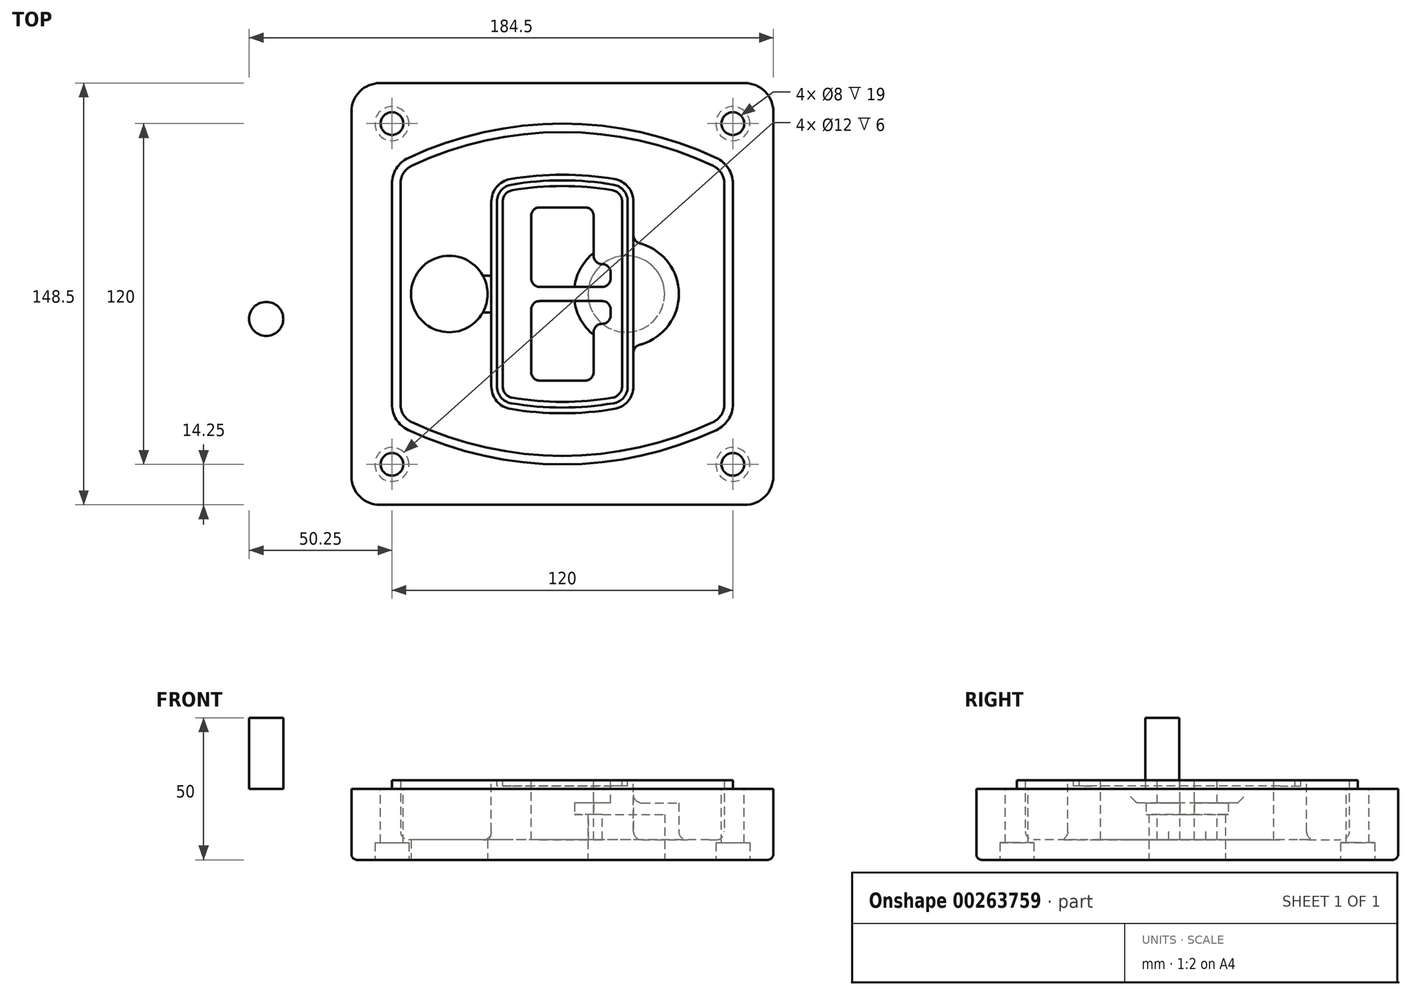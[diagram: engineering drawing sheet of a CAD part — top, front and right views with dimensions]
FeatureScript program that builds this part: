
annotation { "Feature Type Name" : "Feature", "Feature Type Description" : "" }
export const myFeature = defineFeature(function(context is Context, id is Id, definition is map)
    precondition{}
    {
        {
            var Q0;
            Q0=qCreatedBy(makeId("Top.planeOp"),FACE);
            var sketch = newSketch(context, id + "F0", { "sketchPlane" : qUnion([Q0])});
            skPoint(sketch, "E0.rect.middle", {"position": v(0, 0) * mm});
            skLineSegment(sketch, "E1.bottom", {"start": v(-64.25, -74.25) * mm, "end": v(64.25, -74.25) * mm});
            skLineSegment(sketch, "E1.top", {"start": v(-64.25, 74.25) * mm, "end": v(64.25, 74.25) * mm});
            skLineSegment(sketch, "E1.left", {"start": v(-74.25, -64.25) * mm, "end": v(-74.25, 64.25) * mm});
            skLineSegment(sketch, "E1.right", {"start": v(74.25, -64.25) * mm, "end": v(74.25, 64.25) * mm});
            skLineSegment(sketch, "E2", {"start": v(-74.25, 74.25) * mm, "end": v(74.25, -74.25) * mm, "construction": true});
            skLineSegment(sketch, "E3", {"start": v(74.25, 74.25) * mm, "end": v(-74.25, -74.25) * mm, "construction": true});
            skCircle(sketch, "E4", {"center": v(-60, 60) * mm, "radius": 4 * mm});
            skCircle(sketch, "E5", {"center": v(60, 60) * mm, "radius": 4 * mm});
            skCircle(sketch, "E6", {"center": v(60, -60) * mm, "radius": 4 * mm});
            skCircle(sketch, "E7", {"center": v(-60, -60) * mm, "radius": 4 * mm});
            skLineSegment(sketch, "E8", {"start": v(-60, 60) * mm, "end": v(60, 60) * mm, "construction": true});
            skLineSegment(sketch, "E9", {"start": v(60, 60) * mm, "end": v(60, -60) * mm, "construction": true});
            skLineSegment(sketch, "E10", {"start": v(60, -60) * mm, "end": v(-60, -60) * mm, "construction": true});
            skLineSegment(sketch, "E11", {"start": v(-60, -60) * mm, "end": v(-60, 60) * mm, "construction": true});
            skLineSegment(sketch, "E12", {"start": v(-60, 38.83) * mm, "end": v(-60, -38.83) * mm});
            skLineSegment(sketch, "E13", {"start": v(60, 38.83) * mm, "end": v(60, -38.83) * mm});
            skArc(sketch, "E14", {"start": v(54.26, 47.88) * mm, "mid": v(0, 60) * mm, "end": v(-54.26, 47.88) * mm});
            skArc(sketch, "E15", {"start": v(-54.26, -47.88) * mm, "mid": v(0, -60) * mm, "end": v(54.26, -47.88) * mm});
            skLineSegment(sketch, "E16", {"start": v(-60, 0) * mm, "end": v(60, 0) * mm, "construction": true});
            skPoint(sketch, "E17.visualSharp", {"position": v(-60, -45) * mm});
            skArc(sketch, "E17.filletArc", {"start": v(-60, -38.83) * mm, "mid": v(-58.44, -44.2) * mm, "end": v(-54.26, -47.88) * mm});
            skPoint(sketch, "E18.visualSharp", {"position": v(-60, 45) * mm});
            skArc(sketch, "E18.filletArc", {"start": v(-54.26, 47.88) * mm, "mid": v(-58.44, 44.2) * mm, "end": v(-60, 38.83) * mm});
            skPoint(sketch, "E19.visualSharp", {"position": v(60, 45) * mm});
            skArc(sketch, "E19.filletArc", {"start": v(60, 38.83) * mm, "mid": v(58.44, 44.2) * mm, "end": v(54.26, 47.88) * mm});
            skPoint(sketch, "E20.visualSharp", {"position": v(60, -45) * mm});
            skArc(sketch, "E20.filletArc", {"start": v(54.26, -47.88) * mm, "mid": v(58.44, -44.2) * mm, "end": v(60, -38.83) * mm});
            skPoint(sketch, "E21.visualSharp", {"position": v(-74.25, 74.25) * mm});
            skArc(sketch, "E21.filletArc", {"start": v(-64.25, 74.25) * mm, "mid": v(-71.32, 71.32) * mm, "end": v(-74.25, 64.25) * mm});
            skPoint(sketch, "E22.visualSharp", {"position": v(74.25, 74.25) * mm});
            skArc(sketch, "E22.filletArc", {"start": v(74.25, 64.25) * mm, "mid": v(71.32, 71.32) * mm, "end": v(64.25, 74.25) * mm});
            skPoint(sketch, "E23.visualSharp", {"position": v(74.25, -74.25) * mm});
            skArc(sketch, "E23.filletArc", {"start": v(64.25, -74.25) * mm, "mid": v(71.32, -71.32) * mm, "end": v(74.25, -64.25) * mm});
            skPoint(sketch, "E24.visualSharp", {"position": v(-74.25, -74.25) * mm});
            skArc(sketch, "E24.filletArc", {"start": v(-74.25, -64.25) * mm, "mid": v(-71.32, -71.32) * mm, "end": v(-64.25, -74.25) * mm});
            skArc(sketch, "E25.0", {"start": v(57, 38.83) * mm, "mid": v(55.9, 42.58) * mm, "end": v(52.98, 45.17) * mm});
            skLineSegment(sketch, "E25.1", {"start": v(57, 38.83) * mm, "end": v(57, -38.83) * mm});
            skArc(sketch, "E25.2", {"start": v(52.98, -45.17) * mm, "mid": v(55.9, -42.58) * mm, "end": v(57, -38.83) * mm});
            skArc(sketch, "E25.3", {"start": v(-52.98, -45.17) * mm, "mid": v(0, -57) * mm, "end": v(52.98, -45.17) * mm});
            skArc(sketch, "E25.4", {"start": v(-57, -38.83) * mm, "mid": v(-55.9, -42.58) * mm, "end": v(-52.98, -45.17) * mm});
            skArc(sketch, "E25.5", {"start": v(52.98, 45.17) * mm, "mid": v(0, 57) * mm, "end": v(-52.98, 45.17) * mm});
            skLineSegment(sketch, "E25.6", {"start": v(-57, 38.83) * mm, "end": v(-57, -38.83) * mm});
            skArc(sketch, "E25.7", {"start": v(-52.98, 45.17) * mm, "mid": v(-55.9, 42.58) * mm, "end": v(-57, 38.83) * mm});
            skArc(sketch, "E26.0", {"start": v(-55.96, 51.5) * mm, "mid": v(-61.82, 46.33) * mm, "end": v(-64, 38.83) * mm});
            skArc(sketch, "E26.1", {"start": v(55.96, 51.5) * mm, "mid": v(0, 64) * mm, "end": v(-55.96, 51.5) * mm});
            skArc(sketch, "E26.2", {"start": v(64, 38.83) * mm, "mid": v(61.82, 46.33) * mm, "end": v(55.96, 51.5) * mm});
            skLineSegment(sketch, "E26.3", {"start": v(64, 38.83) * mm, "end": v(64, -38.83) * mm});
            skArc(sketch, "E26.4", {"start": v(55.96, -51.5) * mm, "mid": v(61.82, -46.33) * mm, "end": v(64, -38.83) * mm});
            skLineSegment(sketch, "E26.5", {"start": v(-64, 38.83) * mm, "end": v(-64, -38.83) * mm});
            skArc(sketch, "E26.6", {"start": v(-55.96, -51.5) * mm, "mid": v(0, -64) * mm, "end": v(55.96, -51.5) * mm});
            skArc(sketch, "E26.7", {"start": v(-64, -38.83) * mm, "mid": v(-61.82, -46.33) * mm, "end": v(-55.96, -51.5) * mm});
            skSolve(sketch);
        }
        {
            var Q0;
            Q0=makeQuery(id+"F0.imprint","IMPRINT",FACE,{"disambiguationData":[TD([[makeQuery(id+"F0.imprint","IMPRINT",EDGE,{"derivedFrom":sQuery(id+"F0.wireOp",EDGE,"E1.bottom")}),1.0]])]});
            var Q1;
            Q1=makeQuery(id+"F0.imprint","IMPRINT",FACE,{"disambiguationData":[TD([[makeQuery(id+"F0.imprint","IMPRINT",EDGE,{"derivedFrom":sQuery(id+"F0.wireOp",EDGE,"E12")}),1.0]])]});
            var Q2;
            Q2=makeQuery(id+"F0.imprint","IMPRINT",FACE,{"disambiguationData":[TD([[makeQuery(id+"F0.imprint","IMPRINT",EDGE,{"derivedFrom":sQuery(id+"F0.wireOp",EDGE,"E25.0")}),1.0]])]});
            var Q3;
            Q3=makeQuery(id+"F0.imprint","IMPRINT",FACE,{"disambiguationData":[TD([[makeQuery(id+"F0.imprint","IMPRINT",EDGE,{"derivedFrom":sQuery(id+"F0.wireOp",EDGE,"E12")}),-1.0]])]});
            extrude(context, id + "F1", {"entities" : qUnion([Q0, Q1, Q2, Q3]), "oppositeDirection" : true, "depth" : 25 * mm});
        }
        {
            var Q0;
            Q0=makeQuery(id+"F0.imprint","IMPRINT",FACE,{"disambiguationData":[TD([[makeQuery(id+"F0.imprint","IMPRINT",EDGE,{"derivedFrom":sQuery(id+"F0.wireOp",EDGE,"E12")}),1.0]])]});
            extrude(context, id + "F2", {"entities" : qUnion([Q0]), "operationType" : NewBodyOperationType.ADD, "depth" : 3 * mm});
        }
        {
            var Q0;
            Q0=makeQuery(id+"F0.imprint","IMPRINT",FACE,{"disambiguationData":[TD([[makeQuery(id+"F0.imprint","IMPRINT",EDGE,{"derivedFrom":sQuery(id+"F0.wireOp",EDGE,"E25.0")}),1.0]])]});
            extrude(context, id + "F3", {"entities" : qUnion([Q0]), "operationType" : NewBodyOperationType.REMOVE, "oppositeDirection" : true, "depth" : 18 * mm});
        }
        {
            var Q0;
            Q0=makeQuery(id+"F2.opExtrude","CAP_FACE",FACE,{"disambiguationData":[OSD([sQuery(id+"F0.wireOp",EDGE,"E12"),sQuery(id+"F0.wireOp",EDGE,"E13"),sQuery(id+"F0.wireOp",EDGE,"E14"),sQuery(id+"F0.wireOp",EDGE,"E15"),sQuery(id+"F0.wireOp",EDGE,"E17.filletArc"),sQuery(id+"F0.wireOp",EDGE,"E18.filletArc"),sQuery(id+"F0.wireOp",EDGE,"E19.filletArc"),sQuery(id+"F0.wireOp",EDGE,"E20.filletArc"),sQuery(id+"F0.wireOp",EDGE,"E25.0"),sQuery(id+"F0.wireOp",EDGE,"E25.1"),sQuery(id+"F0.wireOp",EDGE,"E25.2"),sQuery(id+"F0.wireOp",EDGE,"E25.3"),sQuery(id+"F0.wireOp",EDGE,"E25.4"),sQuery(id+"F0.wireOp",EDGE,"E25.5"),sQuery(id+"F0.wireOp",EDGE,"E25.6"),sQuery(id+"F0.wireOp",EDGE,"E25.7")])],"isStart":false});
            var sketch = newSketch(context, id + "F4", { "sketchPlane" : qUnion([Q0])});
            skArc(sketch, "E27.0", {"start": v(-18.34, -40.45) * mm, "mid": v(0, -42) * mm, "end": v(18.34, -40.45) * mm});
            skArc(sketch, "E28.0", {"start": v(18.34, 40.45) * mm, "mid": v(0, 42) * mm, "end": v(-18.34, 40.45) * mm});
            skLineSegment(sketch, "E29", {"start": v(-25, 32.57) * mm, "end": v(-25, -32.57) * mm});
            skLineSegment(sketch, "E30", {"start": v(25, 32.57) * mm, "end": v(25, -32.57) * mm});
            skLineSegment(sketch, "E31", {"start": v(-25, 39.1) * mm, "end": v(25, 39.1) * mm, "construction": true});
            skLineSegment(sketch, "E32", {"start": v(-25, -39.1) * mm, "end": v(25, -39.1) * mm, "construction": true});
            skPoint(sketch, "E33.visualSharp", {"position": v(-25, 39.1) * mm});
            skArc(sketch, "E33.filletArc", {"start": v(-18.34, 40.45) * mm, "mid": v(-23.11, 37.73) * mm, "end": v(-25, 32.57) * mm});
            skPoint(sketch, "E34.visualSharp", {"position": v(25, 39.1) * mm});
            skArc(sketch, "E34.filletArc", {"start": v(25, 32.57) * mm, "mid": v(23.11, 37.73) * mm, "end": v(18.34, 40.45) * mm});
            skPoint(sketch, "E35.visualSharp", {"position": v(25, -39.1) * mm});
            skArc(sketch, "E35.filletArc", {"start": v(18.34, -40.45) * mm, "mid": v(23.11, -37.73) * mm, "end": v(25, -32.57) * mm});
            skPoint(sketch, "E36.visualSharp", {"position": v(-25, -39.1) * mm});
            skArc(sketch, "E36.filletArc", {"start": v(-25, -32.57) * mm, "mid": v(-23.11, -37.73) * mm, "end": v(-18.34, -40.45) * mm});
            skArc(sketch, "E37.0", {"start": v(52.98, 45.17) * mm, "mid": v(0, 57) * mm, "end": v(-52.98, 45.17) * mm});
            skArc(sketch, "E37.1", {"start": v(-52.98, 45.17) * mm, "mid": v(-55.9, 42.58) * mm, "end": v(-57, 38.83) * mm});
            skLineSegment(sketch, "E37.2", {"start": v(-57, 38.83) * mm, "end": v(-57, -38.83) * mm});
            skArc(sketch, "E37.3", {"start": v(-57, -38.83) * mm, "mid": v(-55.9, -42.58) * mm, "end": v(-52.98, -45.17) * mm});
            skArc(sketch, "E37.4", {"start": v(-52.98, -45.17) * mm, "mid": v(0, -57) * mm, "end": v(52.98, -45.17) * mm});
            skArc(sketch, "E37.5", {"start": v(52.98, -45.17) * mm, "mid": v(55.9, -42.58) * mm, "end": v(57, -38.83) * mm});
            skLineSegment(sketch, "E37.6", {"start": v(57, 38.83) * mm, "end": v(57, -38.83) * mm});
            skArc(sketch, "E37.7", {"start": v(57, 38.83) * mm, "mid": v(55.9, 42.58) * mm, "end": v(52.98, 45.17) * mm});
            skLineSegment(sketch, "E38.0", {"start": v(23, 32.57) * mm, "end": v(23, -32.57) * mm});
            skArc(sketch, "E38.1", {"start": v(18, -38.48) * mm, "mid": v(21.58, -36.44) * mm, "end": v(23, -32.57) * mm});
            skArc(sketch, "E38.2", {"start": v(-18, -38.48) * mm, "mid": v(0, -40) * mm, "end": v(18, -38.48) * mm});
            skArc(sketch, "E38.3", {"start": v(-23, -32.57) * mm, "mid": v(-21.58, -36.44) * mm, "end": v(-18, -38.48) * mm});
            skLineSegment(sketch, "E38.4", {"start": v(-23, 32.57) * mm, "end": v(-23, -32.57) * mm});
            skArc(sketch, "E38.5", {"start": v(23, 32.57) * mm, "mid": v(21.58, 36.44) * mm, "end": v(18, 38.48) * mm});
            skArc(sketch, "E38.6", {"start": v(-18, 38.48) * mm, "mid": v(-21.58, 36.44) * mm, "end": v(-23, 32.57) * mm});
            skArc(sketch, "E38.7", {"start": v(18, 38.48) * mm, "mid": v(0, 40) * mm, "end": v(-18, 38.48) * mm});
            skArc(sketch, "E39.0", {"start": v(21, 32.57) * mm, "mid": v(20.06, 35.15) * mm, "end": v(17.67, 36.5) * mm});
            skLineSegment(sketch, "E39.1", {"start": v(21, 32.57) * mm, "end": v(21, -32.57) * mm});
            skArc(sketch, "E39.2", {"start": v(17.67, -36.5) * mm, "mid": v(20.06, -35.15) * mm, "end": v(21, -32.57) * mm});
            skArc(sketch, "E39.3", {"start": v(-17.67, -36.5) * mm, "mid": v(0, -38) * mm, "end": v(17.67, -36.5) * mm});
            skArc(sketch, "E39.4", {"start": v(-21, -32.57) * mm, "mid": v(-20.06, -35.15) * mm, "end": v(-17.67, -36.5) * mm});
            skArc(sketch, "E39.5", {"start": v(17.67, 36.5) * mm, "mid": v(0, 38) * mm, "end": v(-17.67, 36.5) * mm});
            skLineSegment(sketch, "E39.6", {"start": v(-21, 32.57) * mm, "end": v(-21, -32.57) * mm});
            skArc(sketch, "E39.7", {"start": v(-17.67, 36.5) * mm, "mid": v(-20.06, 35.15) * mm, "end": v(-21, 32.57) * mm});
            skLineSegment(sketch, "E40", {"start": v(-25, 0) * mm, "end": v(25, 0) * mm, "construction": true});
            skLineSegment(sketch, "E41", {"start": v(-11, 5.5) * mm, "end": v(-11, 27.5) * mm});
            skLineSegment(sketch, "E42", {"start": v(-8, 30.5) * mm, "end": v(8, 30.5) * mm});
            skLineSegment(sketch, "E43", {"start": v(11, 27.5) * mm, "end": v(11, 13.5) * mm});
            skLineSegment(sketch, "E44", {"start": v(14, 10.5) * mm, "end": v(14, 10.5) * mm});
            skLineSegment(sketch, "E45", {"start": v(17, 7.5) * mm, "end": v(17, 5.5) * mm});
            skLineSegment(sketch, "E46", {"start": v(14, 2.5) * mm, "end": v(-8, 2.5) * mm});
            skPoint(sketch, "E47.visualSharp", {"position": v(-11, 30.5) * mm});
            skArc(sketch, "E47.filletArc", {"start": v(-8, 30.5) * mm, "mid": v(-10.12, 29.62) * mm, "end": v(-11, 27.5) * mm});
            skPoint(sketch, "E48.visualSharp", {"position": v(11, 30.5) * mm});
            skArc(sketch, "E48.filletArc", {"start": v(11, 27.5) * mm, "mid": v(10.12, 29.62) * mm, "end": v(8, 30.5) * mm});
            skPoint(sketch, "E49.visualSharp", {"position": v(11, 10.5) * mm});
            skArc(sketch, "E49.filletArc", {"start": v(11, 13.5) * mm, "mid": v(11.88, 11.38) * mm, "end": v(14, 10.5) * mm});
            skPoint(sketch, "E50.visualSharp", {"position": v(17, 10.5) * mm});
            skArc(sketch, "E50.filletArc", {"start": v(17, 7.5) * mm, "mid": v(16.12, 9.62) * mm, "end": v(14, 10.5) * mm});
            skPoint(sketch, "E51.visualSharp", {"position": v(17, 2.5) * mm});
            skArc(sketch, "E51.filletArc", {"start": v(14, 2.5) * mm, "mid": v(16.12, 3.38) * mm, "end": v(17, 5.5) * mm});
            skPoint(sketch, "E52.visualSharp", {"position": v(-11, 2.5) * mm});
            skArc(sketch, "E52.filletArc", {"start": v(-11, 5.5) * mm, "mid": v(-10.12, 3.38) * mm, "end": v(-8, 2.5) * mm});
            skLineSegment(sketch, "E53.0.MirrorCS", {"start": v(14, -2.5) * mm, "end": v(-8, -2.5) * mm});
            skArc(sketch, "E54.0.MirrorCS", {"start": v(-11, -5.5) * mm, "mid": v(-10.12, -3.38) * mm, "end": v(-8, -2.5) * mm});
            skLineSegment(sketch, "E55.0.MirrorCS", {"start": v(-11, -5.5) * mm, "end": v(-11, -27.5) * mm});
            skArc(sketch, "E56.0.MirrorCS", {"start": v(-8, -30.5) * mm, "mid": v(-10.12, -29.62) * mm, "end": v(-11, -27.5) * mm});
            skLineSegment(sketch, "E57.0.MirrorCS", {"start": v(-8, -30.5) * mm, "end": v(8, -30.5) * mm});
            skArc(sketch, "E58.0.MirrorCS", {"start": v(11, -27.5) * mm, "mid": v(10.12, -29.62) * mm, "end": v(8, -30.5) * mm});
            skLineSegment(sketch, "E59.0.MirrorCS", {"start": v(11, -27.5) * mm, "end": v(11, -13.5) * mm});
            skArc(sketch, "E60.0.MirrorCS", {"start": v(11, -13.5) * mm, "mid": v(11.88, -11.38) * mm, "end": v(14, -10.5) * mm});
            skArc(sketch, "E61.0.MirrorCS", {"start": v(17, -7.5) * mm, "mid": v(16.12, -9.62) * mm, "end": v(14, -10.5) * mm});
            skLineSegment(sketch, "E62.0.MirrorCS", {"start": v(17, -7.5) * mm, "end": v(17, -5.5) * mm});
            skArc(sketch, "E63.0.MirrorCS", {"start": v(14, -2.5) * mm, "mid": v(16.12, -3.38) * mm, "end": v(17, -5.5) * mm});
            skSolve(sketch);
        }
        {
            var Q0;
            Q0=makeQuery(id+"F4.imprint","IMPRINT",FACE,{"disambiguationData":[TD([[makeQuery(id+"F4.imprint","IMPRINT",EDGE,{"derivedFrom":sQuery(id+"F4.wireOp",EDGE,"E27.0")}),1.0]])]});
            var Q1;
            Q1=makeQuery(id+"F4.imprint","IMPRINT",FACE,{"disambiguationData":[TD([[makeQuery(id+"F4.imprint","IMPRINT",EDGE,{"derivedFrom":sQuery(id+"F4.wireOp",EDGE,"E38.0")}),-1.0]])]});
            var Q2;
            Q2=makeQuery(id+"F4.imprint","IMPRINT",FACE,{"disambiguationData":[TD([[makeQuery(id+"F4.imprint","IMPRINT",EDGE,{"derivedFrom":sQuery(id+"F4.wireOp",EDGE,"E39.0")}),1.0]])]});
            extrude(context, id + "F5", {"entities" : qUnion([Q0, Q1, Q2]), "operationType" : NewBodyOperationType.ADD, "endBound" : BoundingType.UP_TO_NEXT, "oppositeDirection" : true, "depth" : 25 * mm});
        }
        {
            var Q0;
            Q0=makeQuery(id+"F4.imprint","IMPRINT",FACE,{"disambiguationData":[TD([[makeQuery(id+"F4.imprint","IMPRINT",EDGE,{"derivedFrom":sQuery(id+"F4.wireOp",EDGE,"E38.0")}),-1.0]])]});
            extrude(context, id + "F6", {"entities" : qUnion([Q0]), "operationType" : NewBodyOperationType.REMOVE, "oppositeDirection" : true, "depth" : 2 * mm});
        }
        {
            var Q0;
            Q0=makeQuery(id+"F1.opExtrude","CAP_FACE",FACE,{"disambiguationData":[OSD([sQuery(id+"F0.wireOp",EDGE,"E1.bottom"),sQuery(id+"F0.wireOp",EDGE,"E1.top"),sQuery(id+"F0.wireOp",EDGE,"E1.left"),sQuery(id+"F0.wireOp",EDGE,"E1.right"),sQuery(id+"F0.wireOp",EDGE,"E4"),sQuery(id+"F0.wireOp",EDGE,"E5"),sQuery(id+"F0.wireOp",EDGE,"E6"),sQuery(id+"F0.wireOp",EDGE,"E7"),sQuery(id+"F0.wireOp",EDGE,"E21.filletArc"),sQuery(id+"F0.wireOp",EDGE,"E22.filletArc"),sQuery(id+"F0.wireOp",EDGE,"E23.filletArc"),sQuery(id+"F0.wireOp",EDGE,"E24.filletArc")])],"isStart":false});
            var sketch = newSketch(context, id + "F7", { "sketchPlane" : qUnion([Q0])});
            skCircle(sketch, "E64", {"center": v(22.5, 0) * mm, "radius": 13.47 * mm});
            skCircle(sketch, "E65", {"center": v(-39.81, 0) * mm, "radius": 13.47 * mm});
            skLineSegment(sketch, "E66", {"start": v(74.25, 0) * mm, "end": v(-74.25, 0) * mm});
            skCircle(sketch, "E67", {"center": v(22.5, 0) * mm, "radius": 18.47 * mm});
            skCircle(sketch, "E68", {"center": v(60, -60) * mm, "radius": 6 * mm});
            skCircle(sketch, "E69", {"center": v(-60, -60) * mm, "radius": 6 * mm});
            skCircle(sketch, "E70", {"center": v(-60, 60) * mm, "radius": 6 * mm});
            skCircle(sketch, "E71", {"center": v(60, 60) * mm, "radius": 6 * mm});
            skSolve(sketch);
        }
        {
            var Q0;
            {var subQ1=sQuery(id+"F7.wireOp",EDGE,"E66");var subQ4=sQuery(id+"F7.wireOp",EDGE,"E64");var subQ6=makeQuery(id+"F7.imprint","INTERSECT",VERTEX,{"disambiguationData":[OD(0.0)],"derivedFrom":[subQ4,subQ1]});Q0=makeQuery(id+"F7.imprint","IMPRINT",FACE,{"disambiguationData":[TD([[makeQuery(id+"F7.imprint","IMPRINT",EDGE,{"disambiguationData":[TD([[subQ6,-1.0]])],"derivedFrom":subQ4}),-1.0]])]});}
            var Q1;
            {var subQ0=sQuery(id+"F7.wireOp",EDGE,"E66");var subQ1=sQuery(id+"F7.wireOp",EDGE,"E64");var subQ3=makeQuery(id+"F7.imprint","INTERSECT",VERTEX,{"disambiguationData":[OD(0.0)],"derivedFrom":[subQ1,subQ0]});Q1=makeQuery(id+"F7.imprint","IMPRINT",FACE,{"disambiguationData":[TD([[makeQuery(id+"F7.imprint","IMPRINT",EDGE,{"disambiguationData":[TD([[subQ3,-1.0]])],"derivedFrom":subQ1}),1.0]])]});}
            var Q2;
            {var subQ0=sQuery(id+"F7.wireOp",EDGE,"E66");var subQ1=sQuery(id+"F7.wireOp",EDGE,"E64");var subQ3=makeQuery(id+"F7.imprint","INTERSECT",VERTEX,{"disambiguationData":[OD(0.0)],"derivedFrom":[subQ1,subQ0]});Q2=makeQuery(id+"F7.imprint","IMPRINT",FACE,{"disambiguationData":[TD([[makeQuery(id+"F7.imprint","IMPRINT",EDGE,{"disambiguationData":[TD([[subQ3,1.0]])],"derivedFrom":subQ1}),1.0]])]});}
            var Q3;
            {var subQ1=sQuery(id+"F7.wireOp",EDGE,"E66");var subQ4=sQuery(id+"F7.wireOp",EDGE,"E64");var subQ6=makeQuery(id+"F7.imprint","INTERSECT",VERTEX,{"disambiguationData":[OD(0.0)],"derivedFrom":[subQ4,subQ1]});Q3=makeQuery(id+"F7.imprint","IMPRINT",FACE,{"disambiguationData":[TD([[makeQuery(id+"F7.imprint","IMPRINT",EDGE,{"disambiguationData":[TD([[subQ6,1.0]])],"derivedFrom":subQ4}),-1.0]])]});}
            extrude(context, id + "F8", {"entities" : qUnion([Q0, Q1, Q2, Q3]), "operationType" : NewBodyOperationType.ADD, "oppositeDirection" : true, "depth" : 20 * mm});
        }
        {
            var Q0;
            {var subQ0=sQuery(id+"F7.wireOp",EDGE,"E66");var subQ1=sQuery(id+"F7.wireOp",EDGE,"E64");var subQ3=makeQuery(id+"F7.imprint","INTERSECT",VERTEX,{"disambiguationData":[OD(0.0)],"derivedFrom":[subQ1,subQ0]});Q0=makeQuery(id+"F7.imprint","IMPRINT",FACE,{"disambiguationData":[TD([[makeQuery(id+"F7.imprint","IMPRINT",EDGE,{"disambiguationData":[TD([[subQ3,-1.0]])],"derivedFrom":subQ1}),1.0]])]});}
            var Q1;
            {var subQ0=sQuery(id+"F7.wireOp",EDGE,"E66");var subQ1=sQuery(id+"F7.wireOp",EDGE,"E64");var subQ3=makeQuery(id+"F7.imprint","INTERSECT",VERTEX,{"disambiguationData":[OD(0.0)],"derivedFrom":[subQ1,subQ0]});Q1=makeQuery(id+"F7.imprint","IMPRINT",FACE,{"disambiguationData":[TD([[makeQuery(id+"F7.imprint","IMPRINT",EDGE,{"disambiguationData":[TD([[subQ3,1.0]])],"derivedFrom":subQ1}),1.0]])]});}
            extrude(context, id + "F9", {"entities" : qUnion([Q0, Q1]), "operationType" : NewBodyOperationType.REMOVE, "oppositeDirection" : true, "depth" : 16 * mm});
        }
        {
            var Q0;
            {var subQ0=sQuery(id+"F7.wireOp",EDGE,"E66");var subQ1=sQuery(id+"F7.wireOp",EDGE,"E65");var subQ3=makeQuery(id+"F7.imprint","INTERSECT",VERTEX,{"disambiguationData":[OD(0.0)],"derivedFrom":[subQ1,subQ0]});Q0=makeQuery(id+"F7.imprint","IMPRINT",FACE,{"disambiguationData":[TD([[makeQuery(id+"F7.imprint","IMPRINT",EDGE,{"disambiguationData":[TD([[subQ3,-1.0]])],"derivedFrom":subQ1}),1.0]])]});}
            var Q1;
            {var subQ0=sQuery(id+"F7.wireOp",EDGE,"E66");var subQ1=sQuery(id+"F7.wireOp",EDGE,"E65");var subQ3=makeQuery(id+"F7.imprint","INTERSECT",VERTEX,{"disambiguationData":[OD(0.0)],"derivedFrom":[subQ1,subQ0]});Q1=makeQuery(id+"F7.imprint","IMPRINT",FACE,{"disambiguationData":[TD([[makeQuery(id+"F7.imprint","IMPRINT",EDGE,{"disambiguationData":[TD([[subQ3,1.0]])],"derivedFrom":subQ1}),1.0]])]});}
            extrude(context, id + "F10", {"entities" : qUnion([Q0, Q1]), "operationType" : NewBodyOperationType.REMOVE, "oppositeDirection" : true, "depth" : 25 * mm});
        }
        {
            var Q0;
            Q0=makeQuery(id+"F7.imprint","IMPRINT",FACE,{"disambiguationData":[TD([[makeQuery(id+"F7.imprint","IMPRINT",EDGE,{"derivedFrom":sQuery(id+"F7.wireOp",EDGE,"E68")}),1.0]])]});
            var Q1;
            Q1=makeQuery(id+"F7.imprint","IMPRINT",FACE,{"disambiguationData":[TD([[makeQuery(id+"F7.imprint","IMPRINT",EDGE,{"derivedFrom":makeQuery(id+"F1.opExtrude","CAP_EDGE",EDGE,{"disambiguationData":[OSD([sQuery(id+"F0.wireOp",EDGE,"E5")])],"isStart":false})}),-1.0]])]});
            var Q2;
            Q2=makeQuery(id+"F7.imprint","IMPRINT",FACE,{"disambiguationData":[TD([[makeQuery(id+"F7.imprint","IMPRINT",EDGE,{"derivedFrom":sQuery(id+"F7.wireOp",EDGE,"E69")}),1.0]])]});
            var Q3;
            Q3=makeQuery(id+"F7.imprint","IMPRINT",FACE,{"disambiguationData":[TD([[makeQuery(id+"F7.imprint","IMPRINT",EDGE,{"derivedFrom":makeQuery(id+"F1.opExtrude","CAP_EDGE",EDGE,{"disambiguationData":[OSD([sQuery(id+"F0.wireOp",EDGE,"E4")])],"isStart":false})}),-1.0]])]});
            var Q4;
            Q4=makeQuery(id+"F7.imprint","IMPRINT",FACE,{"disambiguationData":[TD([[makeQuery(id+"F7.imprint","IMPRINT",EDGE,{"derivedFrom":sQuery(id+"F7.wireOp",EDGE,"E70")}),1.0]])]});
            var Q5;
            Q5=makeQuery(id+"F7.imprint","IMPRINT",FACE,{"disambiguationData":[TD([[makeQuery(id+"F7.imprint","IMPRINT",EDGE,{"derivedFrom":makeQuery(id+"F1.opExtrude","CAP_EDGE",EDGE,{"disambiguationData":[OSD([sQuery(id+"F0.wireOp",EDGE,"E7")])],"isStart":false})}),-1.0]])]});
            var Q6;
            Q6=makeQuery(id+"F7.imprint","IMPRINT",FACE,{"disambiguationData":[TD([[makeQuery(id+"F7.imprint","IMPRINT",EDGE,{"derivedFrom":sQuery(id+"F7.wireOp",EDGE,"E71")}),1.0]])]});
            var Q7;
            Q7=makeQuery(id+"F7.imprint","IMPRINT",FACE,{"disambiguationData":[TD([[makeQuery(id+"F7.imprint","IMPRINT",EDGE,{"derivedFrom":makeQuery(id+"F1.opExtrude","CAP_EDGE",EDGE,{"disambiguationData":[OSD([sQuery(id+"F0.wireOp",EDGE,"E6")])],"isStart":false})}),-1.0]])]});
            extrude(context, id + "F11", {"entities" : qUnion([Q0, Q1, Q2, Q3, Q4, Q5, Q6, Q7]), "operationType" : NewBodyOperationType.REMOVE, "oppositeDirection" : true, "depth" : 6 * mm});
        }
        {
            var Q0;
            Q0=makeQuery(id+"F9.boolean.opBoolean","COPY",FACE,{"derivedFrom":makeQuery(id+"F9.opExtrude","CAP_FACE",FACE,{"disambiguationData":[OSD([sQuery(id+"F7.wireOp",EDGE,"E64")])],"isStart":false})});
            var sketch = newSketch(context, id + "F12", { "sketchPlane" : qUnion([Q0])});
            skArc(sketch, "E72.0", {"start": v(11, 14.45) * mm, "mid": v(6.45, 9.13) * mm, "end": v(4.2, 2.5) * mm});
            skArc(sketch, "E72.1", {"start": v(4.2, -2.5) * mm, "mid": v(6.45, -9.13) * mm, "end": v(11, -14.45) * mm});
            skLineSegment(sketch, "E73", {"start": v(4.2, -2.5) * mm, "end": v(14, -2.5) * mm});
            skLineSegment(sketch, "E74.0", {"start": v(14, 2.5) * mm, "end": v(4.2, 2.5) * mm});
            skArc(sketch, "E74.1", {"start": v(14, 2.5) * mm, "mid": v(16.12, 3.38) * mm, "end": v(17, 5.5) * mm});
            skLineSegment(sketch, "E74.2", {"start": v(17, 7.5) * mm, "end": v(17, 5.5) * mm});
            skArc(sketch, "E74.3", {"start": v(17, 7.5) * mm, "mid": v(16.12, 9.62) * mm, "end": v(14, 10.5) * mm});
            skArc(sketch, "E74.4", {"start": v(11, 13.5) * mm, "mid": v(11.88, 11.38) * mm, "end": v(14, 10.5) * mm});
            skLineSegment(sketch, "E74.5", {"start": v(11, 14.45) * mm, "end": v(11, 13.5) * mm});
            skLineSegment(sketch, "E74.7", {"start": v(14, -2.5) * mm, "end": v(4.2, -2.5) * mm});
            skArc(sketch, "E74.8", {"start": v(14, -2.5) * mm, "mid": v(16.12, -3.38) * mm, "end": v(17, -5.5) * mm});
            skLineSegment(sketch, "E74.9", {"start": v(17, -7.5) * mm, "end": v(17, -5.5) * mm});
            skArc(sketch, "E74.10", {"start": v(17, -7.5) * mm, "mid": v(16.12, -9.62) * mm, "end": v(14, -10.5) * mm});
            skArc(sketch, "E74.11", {"start": v(11, -13.5) * mm, "mid": v(11.88, -11.38) * mm, "end": v(14, -10.5) * mm});
            skLineSegment(sketch, "E74.12", {"start": v(11, -14.45) * mm, "end": v(11, -13.5) * mm});
            skPoint(sketch, "E75.orphan", {"position": v(11, -27.5) * mm});
            skPoint(sketch, "E76.orphan", {"position": v(-8, -2.5) * mm});
            skPoint(sketch, "E77.orphan", {"position": v(-8, 2.5) * mm});
            skPoint(sketch, "E78.orphan", {"position": v(11, 27.5) * mm});
            skSolve(sketch);
        }
        {
            var Q0;
            {var subQ7=sQuery(id+"F12.wireOp",EDGE,"E72.0");var subQ14=sQuery(id+"F12.wireOp",EDGE,"E72.1");var subQ16=sQuery(id+"F12.wireOp",EDGE,"E74.1");var subQ18=sQuery(id+"F12.wireOp",EDGE,"E74.8");Q0=qUnion([makeQuery(id+"F12.imprint","IMPRINT",FACE,{"disambiguationData":[TD([[makeQuery(id+"F12.imprint","IMPRINT",EDGE,{"derivedFrom":subQ7}),1.0]])]}),makeQuery(id+"F12.imprint","IMPRINT",FACE,{"disambiguationData":[TD([[makeQuery(id+"F12.imprint","IMPRINT",EDGE,{"derivedFrom":subQ14}),1.0]])]}),makeQuery(id+"F12.imprint","IMPRINT",FACE,{"disambiguationData":[TD([[makeQuery(id+"F12.imprint","IMPRINT",EDGE,{"derivedFrom":subQ16}),1.0]])]}),makeQuery(id+"F12.imprint","IMPRINT",FACE,{"disambiguationData":[TD([[makeQuery(id+"F12.imprint","IMPRINT",EDGE,{"derivedFrom":subQ18}),-1.0]])]})]);}
            var Q1;
            Q1=makeQuery(id+"F5.boolean.opBoolean","SPLIT",FACE,{"disambiguationData":[TD([makeQuery(id+"F5.opExtrude","SWEPT_FACE",FACE,{"disambiguationData":[OSD([sQuery(id+"F4.wireOp",EDGE,"E41")])]})])],"derivedFrom":makeQuery(id+"F3.boolean.opBoolean","COPY",FACE,{"derivedFrom":makeQuery(id+"F3.opExtrude","CAP_FACE",FACE,{"disambiguationData":[OSD([sQuery(id+"F0.wireOp",EDGE,"E25.0"),sQuery(id+"F0.wireOp",EDGE,"E25.1"),sQuery(id+"F0.wireOp",EDGE,"E25.2"),sQuery(id+"F0.wireOp",EDGE,"E25.3"),sQuery(id+"F0.wireOp",EDGE,"E25.4"),sQuery(id+"F0.wireOp",EDGE,"E25.5"),sQuery(id+"F0.wireOp",EDGE,"E25.6"),sQuery(id+"F0.wireOp",EDGE,"E25.7")])],"isStart":false})})});
            extrude(context, id + "F13", {"entities" : qUnion([Q0]), "operationType" : NewBodyOperationType.REMOVE, "endBound" : BoundingType.UP_TO_SURFACE, "endBoundEntityFace" : qUnion([Q1]), "depth" : 25 * mm});
        }
        {
            var Q0;
            Q0=makeQuery(id+"F3.boolean.opBoolean","COPY",EDGE,{"derivedFrom":makeQuery(id+"F3.opExtrude","CAP_EDGE",EDGE,{"disambiguationData":[OSD([sQuery(id+"F0.wireOp",EDGE,"E25.6")])],"isStart":false})});
            var Q1;
            Q1=makeQuery(id+"F8.boolean.opBoolean","INTERSECT",EDGE,{"derivedFrom":[makeQuery(id+"F5.opExtrude","SWEPT_FACE",FACE,{"disambiguationData":[OSD([sQuery(id+"F4.wireOp",EDGE,"E30")])]}),makeQuery(id+"F8.opExtrude","CAP_FACE",FACE,{"disambiguationData":[OSD([sQuery(id+"F7.wireOp",EDGE,"E67")])],"isStart":false})]});
            var Q2;
            Q2=makeQuery(id+"F8.boolean.opBoolean","INTERSECT",EDGE,{"disambiguationData":[OD(1.0)],"derivedFrom":[makeQuery(id+"F5.opExtrude","SWEPT_FACE",FACE,{"disambiguationData":[OSD([sQuery(id+"F4.wireOp",EDGE,"E30")])]}),makeQuery(id+"F8.opExtrude","SWEPT_FACE",FACE,{"disambiguationData":[OSD([sQuery(id+"F7.wireOp",EDGE,"E67")])]})]});
            var Q3;
            {var subQ0=sQuery(id+"F4.wireOp",EDGE,"E30");Q3=makeQuery(id+"F8.boolean.opBoolean","SPLIT",EDGE,{"disambiguationData":[TD([makeQuery(id+"F5.opExtrude","SWEPT_FACE",FACE,{"disambiguationData":[OSD([sQuery(id+"F4.wireOp",EDGE,"E35.filletArc")])]})])],"derivedFrom":makeQuery(id+"F5.opExtrude","CAP_EDGE",EDGE,{"disambiguationData":[OSD([subQ0])],"isStart":false})});}
            var Q4;
            {var subQ0=sQuery(id+"F0.wireOp",EDGE,"E25.7");var subQ1=sQuery(id+"F0.wireOp",EDGE,"E25.1");var subQ2=sQuery(id+"F0.wireOp",EDGE,"E25.6");var subQ3=sQuery(id+"F0.wireOp",EDGE,"E25.5");var subQ4=sQuery(id+"F0.wireOp",EDGE,"E25.4");var subQ5=sQuery(id+"F0.wireOp",EDGE,"E25.0");var subQ6=sQuery(id+"F0.wireOp",EDGE,"E25.2");var subQ7=sQuery(id+"F0.wireOp",EDGE,"E25.3");Q4=makeQuery(id+"F8.boolean.opBoolean","INTERSECT",EDGE,{"derivedFrom":[makeQuery(id+"F5.boolean.opBoolean","SPLIT",FACE,{"disambiguationData":[TD([makeQuery(id+"F2.opExtrude","SWEPT_FACE",FACE,{"disambiguationData":[OSD([subQ5])]})])],"derivedFrom":makeQuery(id+"F3.boolean.opBoolean","COPY",FACE,{"derivedFrom":makeQuery(id+"F3.opExtrude","CAP_FACE",FACE,{"disambiguationData":[OSD([subQ5,subQ1,subQ6,subQ7,subQ4,subQ3,subQ2,subQ0])],"isStart":false})})}),makeQuery(id+"F8.opExtrude","SWEPT_FACE",FACE,{"disambiguationData":[OSD([sQuery(id+"F7.wireOp",EDGE,"E67")])]})]});}
            var Q5;
            Q5=makeQuery(id+"F8.boolean.opBoolean","INTERSECT",EDGE,{"disambiguationData":[OD(0.0)],"derivedFrom":[makeQuery(id+"F5.opExtrude","SWEPT_FACE",FACE,{"disambiguationData":[OSD([sQuery(id+"F4.wireOp",EDGE,"E30")])]}),makeQuery(id+"F8.opExtrude","SWEPT_FACE",FACE,{"disambiguationData":[OSD([sQuery(id+"F7.wireOp",EDGE,"E67")])]})]});
            fillet(context, id + "F14", {"entities" : qUnion([Q0, Q1, Q2, Q3, Q4, Q5]), "radius" : 3 * mm, "tangentPropagation" : true, "allowEdgeOverflow" : false});
        }
        {
            var Q0;
            Q0=makeQuery(id+"F1.opExtrude","CAP_EDGE",EDGE,{"disambiguationData":[OSD([sQuery(id+"F0.wireOp",EDGE,"E1.bottom")])],"isStart":false});
            fillet(context, id + "F15", {"entities" : qUnion([Q0]), "radius" : 2 * mm, "tangentPropagation" : true, "allowEdgeOverflow" : false});
        }
        {
            var Q0;
            {var subQ0=sQuery(id+"F0.wireOp",EDGE,"E22.filletArc");var subQ1=sQuery(id+"F0.wireOp",EDGE,"E7");var subQ2=sQuery(id+"F0.wireOp",EDGE,"E6");var subQ3=sQuery(id+"F0.wireOp",EDGE,"E5");var subQ4=sQuery(id+"F0.wireOp",EDGE,"E4");var subQ5=sQuery(id+"F0.wireOp",EDGE,"E1.bottom");var subQ6=sQuery(id+"F0.wireOp",EDGE,"E21.filletArc");var subQ7=sQuery(id+"F0.wireOp",EDGE,"E1.top");var subQ8=sQuery(id+"F0.wireOp",EDGE,"E1.left");var subQ9=sQuery(id+"F0.wireOp",EDGE,"E1.right");var subQ10=sQuery(id+"F0.wireOp",EDGE,"E23.filletArc");var subQ11=sQuery(id+"F0.wireOp",EDGE,"E24.filletArc");Q0=makeQuery(id+"F2.boolean.opBoolean","SPLIT",FACE,{"disambiguationData":[TD([makeQuery(id+"F1.opExtrude","SWEPT_FACE",FACE,{"disambiguationData":[OSD([subQ5])]})])],"derivedFrom":makeQuery(id+"F1.opExtrude","CAP_FACE",FACE,{"disambiguationData":[OSD([subQ5,subQ7,subQ8,subQ9,subQ4,subQ3,subQ2,subQ1,subQ6,subQ0,subQ10,subQ11])],"isStart":true})});}
            var sketch = newSketch(context, id + "F16", { "sketchPlane" : qUnion([Q0])});
            skLineSegment(sketch, "E79", {"start": v(-74.25, 12.58) * mm, "end": v(-91.08, 6.2) * mm});
            skLineSegment(sketch, "E80", {"start": v(-74.25, -30.17) * mm, "end": v(-91.08, -23.78) * mm});
            skLineSegment(sketch, "E81", {"start": v(-91.08, -23.78) * mm, "end": v(-104.25, -23.78) * mm});
            skLineSegment(sketch, "E82", {"start": v(-91.08, 6.2) * mm, "end": v(-103.53, 6.2) * mm});
            skArc(sketch, "E83", {"start": v(-103.53, 6.2) * mm, "mid": v(-119.25, -8.42) * mm, "end": v(-104.25, -23.78) * mm});
            skCircle(sketch, "E84", {"center": v(-104.25, -8.78) * mm, "radius": 6 * mm});
            skSolve(sketch);
        }
        {
            var Q0;
            Q0 = qSketchRegion(id + "F16", true);
            extrude(context, id + "F17", {"entities" : qUnion([Q0]), "depth" : 25 * mm});
        }
    });
